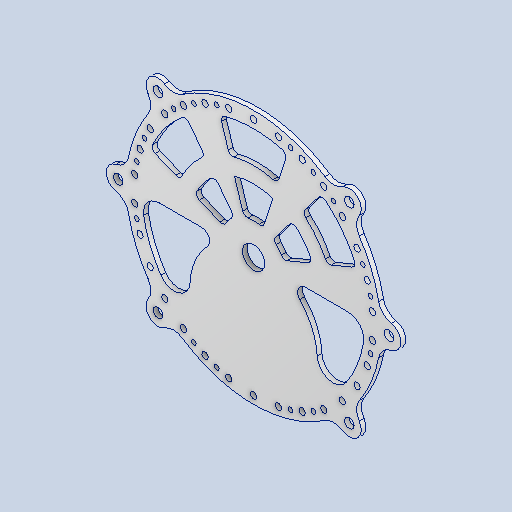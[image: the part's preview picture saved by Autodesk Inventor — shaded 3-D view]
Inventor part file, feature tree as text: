
AUTODESK INVENTOR PART (.ipt)
format: ipt  version: 2024 (Build 280153000, 153)  size: 404,480 bytes
history: native  units: mm
features: thread x16, sketch x8, extrude x4, hole x4, pattern_circular x2, other x1, fillet x1
ambient origin geometry x8: Origin, YZ Plane, XZ Plane, XY Plane, X Axis, Y Axis, Z Axis, Center Point
bodies: Body1 (feature_tree)
feature tree (36):
  other  "ソリッド1"
  extrude  "押し出し1"  Depth=160.0mm
  hole  "穴1"  [1 undecoded]
  pattern_circular  "円形状パターン1"  Count=15  [1 undecoded]
  hole  "穴2"  [1 undecoded]
  hole  "穴3"  [1 undecoded]
  thread  "ねじ1"
  thread  "ねじ2"
  thread  "ねじ3"
  thread  "ねじ4"
  thread  "ねじ5"
  thread  "ねじ6"
  thread  "ねじ7"
  thread  "ねじ8"
  thread  "ねじ9"
  thread  "ねじ10"
  thread  "ねじ11"
  thread  "ねじ12"
  thread  "ねじ13"
  thread  "ねじ14"
  thread  "ねじ15"
  thread  "ねじ16"
  extrude  "押し出し2"  Depth=150.0mm
  hole  "穴4"  [1 undecoded]
  pattern_circular  "円形状パターン2"  Count=6 Angle=60.0deg
  extrude  "押し出し3"  Depth=3.0mm TaperAngle=0.0deg
  extrude  "押し出し4"  Depth=3.0mm TaperAngle=0.0deg
  fillet  "フィレット1"  Radius=3.0mm
  sketch  "スケッチ1"
  sketch  "スケッチ2"
  sketch  "スケッチ3"
  sketch  "スケッチ4"
  sketch  "スケッチ5"
  sketch  "スケッチ6"
  sketch  "スケッチ7"
  sketch  "スケッチ8"
note: 5 required parameter values undecoded (feature->parameter linkage not recoverable at this tier; creation-order binding heuristic only, values carry confidence <= 0.55)
